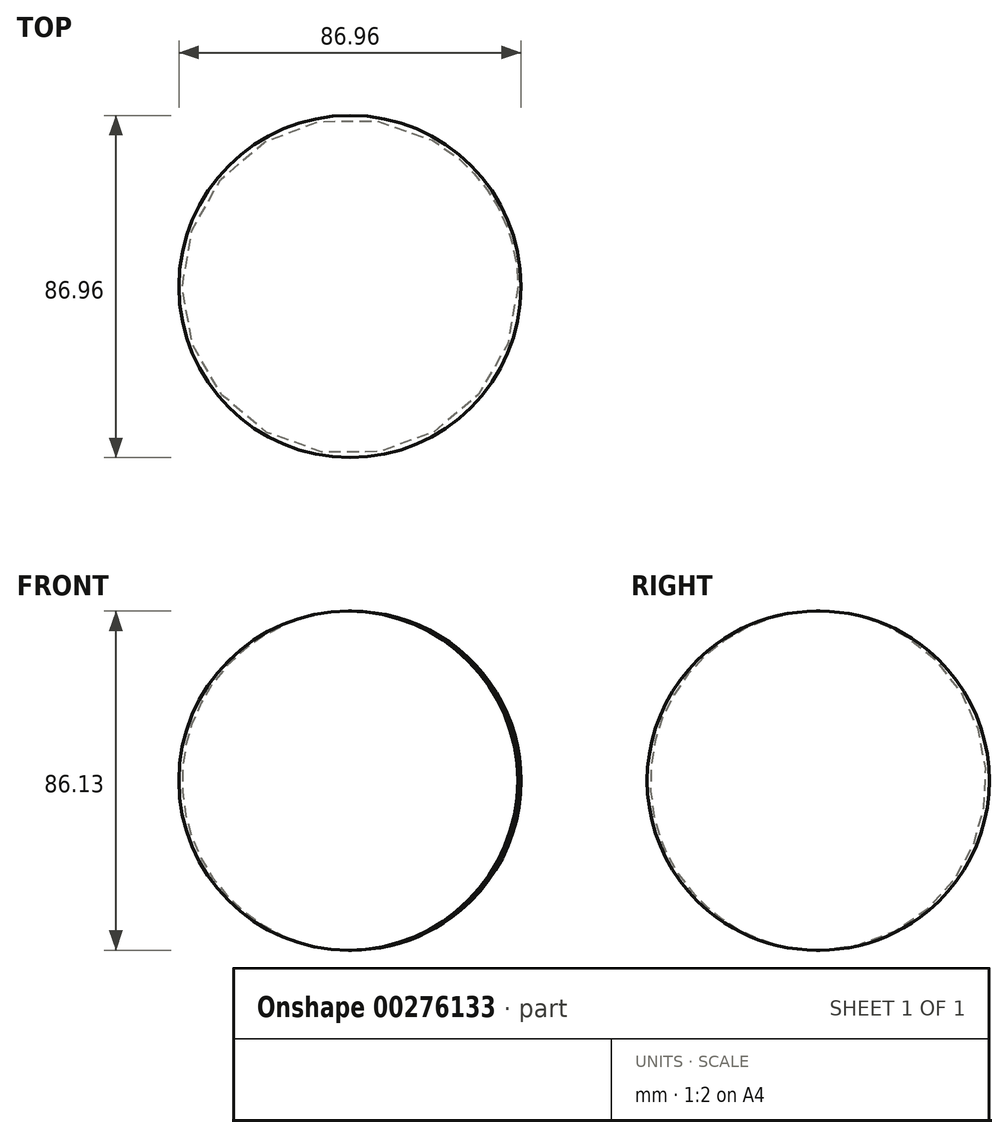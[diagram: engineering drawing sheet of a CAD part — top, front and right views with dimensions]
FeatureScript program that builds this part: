
annotation { "Feature Type Name" : "Feature", "Feature Type Description" : "" }
export const myFeature = defineFeature(function(context is Context, id is Id, definition is map)
    precondition{}
    {
        {
            var Q0;
            Q0=qCreatedBy(makeId("Front.planeOp"),FACE);
            var sketch = newSketch(context, id + "F0", { "sketchPlane" : qUnion([Q0])});
            skLineSegment(sketch, "E0", {"start": v(0, 75.3) * mm, "end": v(0, -76.48) * mm, "construction": true});
            skArc(sketch, "E1", {"start": v(0, 42.56) * mm, "mid": v(-42.65, -0.5) * mm, "end": v(0, -43.56) * mm});
            skLineSegment(sketch, "E2", {"start": v(0, 42.56) * mm, "end": v(0, -43.56) * mm});
            skSolve(sketch);
        }
        {
            var Q0;
            Q0 = qSketchRegion(id + "F0", true);
            var Q1;
            Q1=sQuery(id+"F0.wireOp",EDGE,"E0");
            revolve(context, id + "F1", {"entities" : qUnion([Q0]), "axis" : qUnion([Q1]), "revolveType" : RevolveType.FULL, "oppositeDirection" : true});
        }
    });
